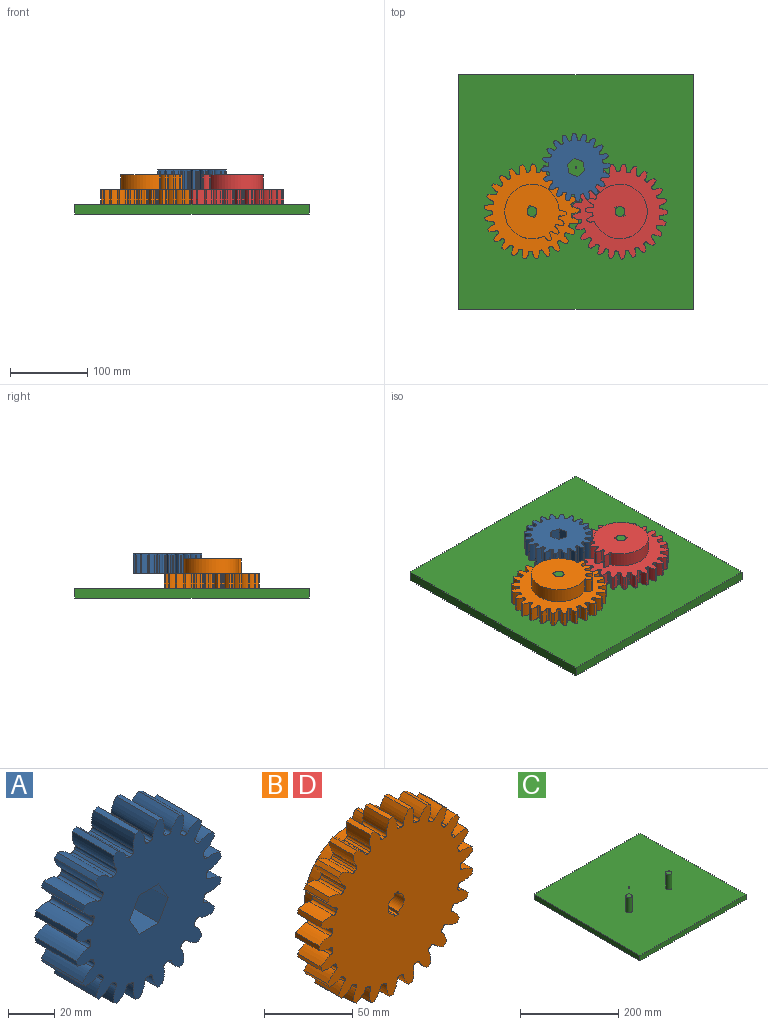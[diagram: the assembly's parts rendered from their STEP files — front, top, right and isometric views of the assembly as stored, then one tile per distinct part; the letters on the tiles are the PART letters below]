
ASSEMBLY  parts=4 mates=3
PART A: 128 faces, bbox 88.3x25.4x88.3 mm
  f0: plane 88.27x88.27mm, normal (0,-1,0), area 4657.8mm2, adj f2,f3,f4,f5,f6,f7,f8,f9
  f1: plane 88.27x88.27mm, normal (0,1,0), area 4657.8mm2, adj f2,f3,f4,f5,f6,f7,f8,f9
  f2: extruded ~25.4x7.35mm, area 207.9mm2, adj f0,f1,f81,f82
  f3: cylinder r=35.36mm len=25.4mm, axis (0,1,0), area 41mm2, adj f0,f1,f82,f83
  f4: extruded ~25.4x7.35mm, area 207.9mm2, adj f0,f1,f5,f83
  f5: cylinder r=44.45mm len=25.4mm, axis (0,1,0), area 71.3mm2, adj f0,f1,f4,f6
  f6: extruded ~25.4x7.98mm, area 207.9mm2, adj f0,f1,f5,f84
  f7: cylinder r=35.36mm len=25.4mm, axis (0,1,0), area 41mm2, adj f0,f1,f84,f85
  f8: extruded ~25.4x5.99mm, area 207.9mm2, adj f0,f1,f9,f85
  f9: cylinder r=44.45mm len=25.4mm, axis (0,1,0), area 71.3mm2, adj f0,f1,f8,f10
  f10: extruded ~25.4x7.84mm, area 207.9mm2, adj f0,f1,f9,f86
  f11: cylinder r=35.36mm len=25.4mm, axis (0,1,0), area 41mm2, adj f0,f1,f86,f87
  f12: extruded ~25.4x6.93mm, area 207.9mm2, adj f0,f1,f13,f87
  f13: cylinder r=44.45mm len=25.4mm, axis (0,1,0), area 71.3mm2, adj f0,f1,f12,f14
  f14: extruded ~25.4x6.93mm, area 207.9mm2, adj f0,f1,f13,f88
  f15: cylinder r=35.36mm len=25.4mm, axis (0,1,0), area 41mm2, adj f0,f1,f88,f89
  f16: extruded ~25.4x7.84mm, area 207.9mm2, adj f0,f1,f17,f89
  f17: cylinder r=44.45mm len=25.4mm, axis (0,1,0), area 71.3mm2, adj f0,f1,f16,f18
  f18: extruded ~25.4x5.99mm, area 207.9mm2, adj f0,f1,f17,f90
  f19: cylinder r=35.36mm len=25.4mm, axis (0,1,0), area 41mm2, adj f0,f1,f90,f91
  f20: extruded ~25.4x7.98mm, area 207.9mm2, adj f0,f1,f21,f91
  f21: cylinder r=44.45mm len=25.4mm, axis (0,1,0), area 71.3mm2, adj f0,f1,f20,f22
  f22: extruded ~25.4x7.35mm, area 207.9mm2, adj f0,f1,f21,f92
  f23: cylinder r=35.36mm len=25.4mm, axis (0,1,0), area 41mm2, adj f0,f1,f92,f93
  f24: extruded ~25.4x7.35mm, area 207.9mm2, adj f0,f1,f25,f93
  f25: cylinder r=44.45mm len=25.4mm, axis (0,1,0), area 71.3mm2, adj f0,f1,f24,f26
  f26: extruded ~25.4x7.98mm, area 207.9mm2, adj f0,f1,f25,f94
  f27: cylinder r=35.36mm len=25.4mm, axis (0,1,0), area 41mm2, adj f0,f1,f94,f95
  f28: extruded ~25.4x5.99mm, area 207.9mm2, adj f0,f1,f29,f95
  f29: cylinder r=44.45mm len=25.4mm, axis (0,1,0), area 71.3mm2, adj f0,f1,f28,f30
  f30: extruded ~25.4x7.84mm, area 207.9mm2, adj f0,f1,f29,f96
  f31: cylinder r=35.36mm len=25.4mm, axis (0,1,0), area 41mm2, adj f0,f1,f96,f97
  f32: extruded ~25.4x6.93mm, area 207.9mm2, adj f0,f1,f33,f97
  f33: cylinder r=44.45mm len=25.4mm, axis (0,1,0), area 71.3mm2, adj f0,f1,f32,f34
  f34: extruded ~25.4x6.93mm, area 207.9mm2, adj f0,f1,f33,f98
  f35: cylinder r=35.36mm len=25.4mm, axis (0,1,0), area 41mm2, adj f0,f1,f98,f99
  f36: extruded ~25.4x7.84mm, area 207.9mm2, adj f0,f1,f37,f99
  f37: cylinder r=44.45mm len=25.4mm, axis (0,1,0), area 71.3mm2, adj f0,f1,f36,f38
  f38: extruded ~25.4x5.99mm, area 207.9mm2, adj f0,f1,f37,f100
  f39: cylinder r=35.36mm len=25.4mm, axis (0,1,0), area 41mm2, adj f0,f1,f100,f101
  f40: extruded ~25.4x7.98mm, area 207.9mm2, adj f0,f1,f41,f101
  f41: cylinder r=44.45mm len=25.4mm, axis (0,1,0), area 71.3mm2, adj f0,f1,f40,f42
  f42: extruded ~25.4x7.35mm, area 207.9mm2, adj f0,f1,f41,f102
  f43: cylinder r=35.36mm len=25.4mm, axis (0,1,0), area 41mm2, adj f0,f1,f102,f103
  f44: extruded ~25.4x7.35mm, area 207.9mm2, adj f0,f1,f45,f103
  f45: cylinder r=44.45mm len=25.4mm, axis (0,1,0), area 71.3mm2, adj f0,f1,f44,f46
  f46: extruded ~25.4x7.98mm, area 207.9mm2, adj f0,f1,f45,f104
  f47: cylinder r=35.36mm len=25.4mm, axis (0,1,0), area 41mm2, adj f0,f1,f104,f105
  f48: extruded ~25.4x5.99mm, area 207.9mm2, adj f0,f1,f49,f105
  f49: cylinder r=44.45mm len=25.4mm, axis (0,1,0), area 71.3mm2, adj f0,f1,f48,f50
  f50: extruded ~25.4x7.84mm, area 207.9mm2, adj f0,f1,f49,f106
  f51: cylinder r=35.36mm len=25.4mm, axis (0,1,0), area 41mm2, adj f0,f1,f106,f107
  f52: extruded ~25.4x6.93mm, area 207.9mm2, adj f0,f1,f53,f107
  f53: cylinder r=44.45mm len=25.4mm, axis (0,1,0), area 71.3mm2, adj f0,f1,f52,f54
  f54: extruded ~25.4x6.93mm, area 207.9mm2, adj f0,f1,f53,f108
  f55: cylinder r=35.36mm len=25.4mm, axis (0,1,0), area 41mm2, adj f0,f1,f108,f109
  f56: extruded ~25.4x7.84mm, area 207.9mm2, adj f0,f1,f57,f109
  f57: cylinder r=44.45mm len=25.4mm, axis (0,1,0), area 71.3mm2, adj f0,f1,f56,f58
  f58: extruded ~25.4x5.99mm, area 207.9mm2, adj f0,f1,f57,f110
  f59: cylinder r=35.36mm len=25.4mm, axis (0,1,0), area 41mm2, adj f0,f1,f110,f111
  f60: extruded ~25.4x7.98mm, area 207.9mm2, adj f0,f1,f61,f111
  f61: cylinder r=44.45mm len=25.4mm, axis (0,1,0), area 71.3mm2, adj f0,f1,f60,f62
  f62: extruded ~25.4x7.35mm, area 207.9mm2, adj f0,f1,f61,f112
  f63: cylinder r=35.36mm len=25.4mm, axis (0,1,0), area 41mm2, adj f0,f1,f112,f113
  f64: extruded ~25.4x7.35mm, area 207.9mm2, adj f0,f1,f65,f113
  f65: cylinder r=44.45mm len=25.4mm, axis (0,1,0), area 71.3mm2, adj f0,f1,f64,f66
  f66: extruded ~25.4x7.98mm, area 207.9mm2, adj f0,f1,f65,f114
  f67: cylinder r=35.36mm len=25.4mm, axis (0,1,0), area 41mm2, adj f0,f1,f114,f115
  f68: extruded ~25.4x5.99mm, area 207.9mm2, adj f0,f1,f69,f115
  f69: cylinder r=44.45mm len=25.4mm, axis (0,1,0), area 71.3mm2, adj f0,f1,f68,f70
  f70: extruded ~25.4x7.84mm, area 207.9mm2, adj f0,f1,f69,f116
  f71: cylinder r=35.36mm len=25.4mm, axis (0,1,0), area 41mm2, adj f0,f1,f116,f117
  f72: extruded ~25.4x6.93mm, area 207.9mm2, adj f0,f1,f73,f117
  f73: cylinder r=44.45mm len=25.4mm, axis (0,1,0), area 71.3mm2, adj f0,f1,f72,f74
  f74: extruded ~25.4x6.93mm, area 207.9mm2, adj f0,f1,f73,f118
  f75: cylinder r=35.36mm len=25.4mm, axis (0,1,0), area 41mm2, adj f0,f1,f118,f119
  f76: extruded ~25.4x7.84mm, area 207.9mm2, adj f0,f1,f77,f119
  f77: cylinder r=44.45mm len=25.4mm, axis (0,1,0), area 71.3mm2, adj f0,f1,f76,f78
  f78: extruded ~25.4x5.99mm, area 207.9mm2, adj f0,f1,f77,f120
  f79: cylinder r=35.36mm len=25.4mm, axis (0,1,0), area 41mm2, adj f0,f1,f120,f121
  f80: extruded ~25.4x7.98mm, area 207.9mm2, adj f0,f1,f81,f121
  f81: cylinder r=44.45mm len=25.4mm, axis (0,1,0), area 71.3mm2, adj f0,f1,f2,f80
  f82: cylinder r=1.5mm len=25.4mm, axis (0,1,0), area 58.3mm2, adj f0,f1,f2,f3
  f83: cylinder r=1.5mm len=25.4mm, axis (0,1,0), area 58.3mm2, adj f0,f1,f3,f4
  f84: cylinder r=1.5mm len=25.4mm, axis (0,1,0), area 58.3mm2, adj f0,f1,f6,f7
  f85: cylinder r=1.5mm len=25.4mm, axis (0,1,0), area 58.3mm2, adj f0,f1,f7,f8
  f86: cylinder r=1.5mm len=25.4mm, axis (0,1,0), area 58.3mm2, adj f0,f1,f10,f11
  f87: cylinder r=1.5mm len=25.4mm, axis (0,1,0), area 58.3mm2, adj f0,f1,f11,f12
  f88: cylinder r=1.5mm len=25.4mm, axis (0,1,0), area 58.3mm2, adj f0,f1,f14,f15
  f89: cylinder r=1.5mm len=25.4mm, axis (0,1,0), area 58.3mm2, adj f0,f1,f15,f16
  f90: cylinder r=1.5mm len=25.4mm, axis (0,1,0), area 58.3mm2, adj f0,f1,f18,f19
  f91: cylinder r=1.5mm len=25.4mm, axis (0,1,0), area 58.3mm2, adj f0,f1,f19,f20
  f92: cylinder r=1.5mm len=25.4mm, axis (0,1,0), area 58.3mm2, adj f0,f1,f22,f23
  f93: cylinder r=1.5mm len=25.4mm, axis (0,1,0), area 58.3mm2, adj f0,f1,f23,f24
  f94: cylinder r=1.5mm len=25.4mm, axis (0,1,0), area 58.3mm2, adj f0,f1,f26,f27
  f95: cylinder r=1.5mm len=25.4mm, axis (0,1,0), area 58.3mm2, adj f0,f1,f27,f28
  f96: cylinder r=1.5mm len=25.4mm, axis (0,1,0), area 58.3mm2, adj f0,f1,f30,f31
  f97: cylinder r=1.5mm len=25.4mm, axis (0,1,0), area 58.3mm2, adj f0,f1,f31,f32
  f98: cylinder r=1.5mm len=25.4mm, axis (0,1,0), area 58.3mm2, adj f0,f1,f34,f35
  f99: cylinder r=1.5mm len=25.4mm, axis (0,1,0), area 58.3mm2, adj f0,f1,f35,f36
  f100: cylinder r=1.5mm len=25.4mm, axis (0,1,0), area 58.3mm2, adj f0,f1,f38,f39
  f101: cylinder r=1.5mm len=25.4mm, axis (0,1,0), area 58.3mm2, adj f0,f1,f39,f40
  f102: cylinder r=1.5mm len=25.4mm, axis (0,1,0), area 58.3mm2, adj f0,f1,f42,f43
  f103: cylinder r=1.5mm len=25.4mm, axis (0,1,0), area 58.3mm2, adj f0,f1,f43,f44
  f104: cylinder r=1.5mm len=25.4mm, axis (0,1,0), area 58.3mm2, adj f0,f1,f46,f47
  f105: cylinder r=1.5mm len=25.4mm, axis (0,1,0), area 58.3mm2, adj f0,f1,f47,f48
  f106: cylinder r=1.5mm len=25.4mm, axis (0,1,0), area 58.3mm2, adj f0,f1,f50,f51
  f107: cylinder r=1.5mm len=25.4mm, axis (0,1,0), area 58.3mm2, adj f0,f1,f51,f52
  f108: cylinder r=1.5mm len=25.4mm, axis (0,1,0), area 58.3mm2, adj f0,f1,f54,f55
  f109: cylinder r=1.5mm len=25.4mm, axis (0,1,0), area 58.3mm2, adj f0,f1,f55,f56
  f110: cylinder r=1.5mm len=25.4mm, axis (0,1,0), area 58.3mm2, adj f0,f1,f58,f59
  f111: cylinder r=1.5mm len=25.4mm, axis (0,1,0), area 58.3mm2, adj f0,f1,f59,f60
  f112: cylinder r=1.5mm len=25.4mm, axis (0,1,0), area 58.3mm2, adj f0,f1,f62,f63
  f113: cylinder r=1.5mm len=25.4mm, axis (0,1,0), area 58.3mm2, adj f0,f1,f63,f64
  f114: cylinder r=1.5mm len=25.4mm, axis (0,1,0), area 58.3mm2, adj f0,f1,f66,f67
  f115: cylinder r=1.5mm len=25.4mm, axis (0,1,0), area 58.3mm2, adj f0,f1,f67,f68
  f116: cylinder r=1.5mm len=25.4mm, axis (0,1,0), area 58.3mm2, adj f0,f1,f70,f71
  f117: cylinder r=1.5mm len=25.4mm, axis (0,1,0), area 58.3mm2, adj f0,f1,f71,f72
  f118: cylinder r=1.5mm len=25.4mm, axis (0,1,0), area 58.3mm2, adj f0,f1,f74,f75
  f119: cylinder r=1.5mm len=25.4mm, axis (0,1,0), area 58.3mm2, adj f0,f1,f75,f76
  f120: cylinder r=1.5mm len=25.4mm, axis (0,1,0), area 58.3mm2, adj f0,f1,f78,f79
  f121: cylinder r=1.5mm len=25.4mm, axis (0,1,0), area 58.3mm2, adj f0,f1,f79,f80
  f122: plane 25.4x11.88mm, normal (0,0,-1), area 301.7mm2, adj f0,f1,f123,f127
  f123: plane 25.4x10.29mm, normal (-0.87,0,-0.5), area 301.7mm2, adj f0,f1,f122,f124
  f124: plane 25.4x10.29mm, normal (-0.87,0,0.5), area 301.7mm2, adj f0,f1,f123,f125
  f125: plane 25.4x11.88mm, normal (0,0,1), area 301.7mm2, adj f0,f1,f124,f126
  f126: plane 25.4x10.29mm, normal (0.87,0,0.5), area 301.7mm2, adj f0,f1,f125,f127
  f127: plane 25.4x10.29mm, normal (0.87,0,-0.5), area 301.7mm2, adj f0,f1,f122,f126
PART B: 185 faces, bbox 123.2x38.1x123.4 mm
  f0: plane 79.49x75.61mm, normal (0,1,0), area 4006.1mm2, adj f1,f2,f3,f4,f5,f6,f7,f8
  f1: extruded ~19.05x5.99mm, area 155.9mm2, adj f0,f2,f17,f33
  f2: cylinder r=44.45mm len=19.05mm, axis (0,-1,0), area 53.5mm2, adj f0,f1,f3,f33
  f3: extruded ~19.05x7.84mm, area 155.9mm2, adj f0,f2,f18,f33
  f4: cylinder r=35.36mm len=19.05mm, axis (0,-1,0), area 30.7mm2, adj f0,f18,f19,f33
  f5: extruded ~19.05x6.93mm, area 155.9mm2, adj f0,f6,f19,f33
  f6: cylinder r=44.45mm len=19.05mm, axis (0,-1,0), area 53.5mm2, adj f0,f5,f7,f33
  f7: extruded ~19.05x6.93mm, area 155.9mm2, adj f0,f6,f20,f33
  f8: cylinder r=35.36mm len=19.05mm, axis (0,-1,0), area 30.7mm2, adj f0,f20,f21,f33
  f9: extruded ~19.05x7.84mm, area 155.9mm2, adj f0,f10,f21,f33
  f10: cylinder r=44.45mm len=19.05mm, axis (0,-1,0), area 53.5mm2, adj f0,f9,f11,f33
  f11: extruded ~19.05x5.99mm, area 155.9mm2, adj f0,f10,f22,f33
  f12: cylinder r=35.36mm len=19.05mm, axis (0,-1,0), area 30.7mm2, adj f0,f22,f23,f33
  f13: extruded ~19.05x7.98mm, area 155.9mm2, adj f0,f14,f23,f33
  f14: cylinder r=44.45mm len=19.05mm, axis (0,-1,0), area 53.5mm2, adj f0,f13,f15,f33
  f15: extruded ~19.05x7.35mm, area 155.9mm2, adj f0,f14,f24,f33
  f16: cylinder r=35.36mm len=70.72mm, axis (0,-1,0), area 3416.6mm2, adj f0,f17,f24,f33
  f17: cylinder r=1.5mm len=19.05mm, axis (0,-1,0), area 43.7mm2, adj f0,f1,f16,f33
  f18: cylinder r=1.5mm len=19.05mm, axis (0,-1,0), area 43.7mm2, adj f0,f3,f4,f33
  f19: cylinder r=1.5mm len=19.05mm, axis (0,-1,0), area 43.7mm2, adj f0,f4,f5,f33
  f20: cylinder r=1.5mm len=19.05mm, axis (0,-1,0), area 43.7mm2, adj f0,f7,f8,f33
  f21: cylinder r=1.5mm len=19.05mm, axis (0,-1,0), area 43.7mm2, adj f0,f8,f9,f33
  f22: cylinder r=1.5mm len=19.05mm, axis (0,-1,0), area 43.7mm2, adj f0,f11,f12,f33
  f23: cylinder r=1.5mm len=19.05mm, axis (0,-1,0), area 43.7mm2, adj f0,f12,f13,f33
  f24: cylinder r=1.5mm len=19.05mm, axis (0,-1,0), area 43.7mm2, adj f0,f15,f16,f33
  f25: plane 38.1x1.69mm, normal (-1,0,0), area 64.3mm2, adj f0,f26,f32,f34
  f26: cylinder r=6.45mm len=38.1mm, axis (0,1,0), area 646.1mm2, adj f0,f25,f27,f34
  f27: plane 38.1x1.69mm, normal (-1,0,0), area 64.3mm2, adj f0,f26,f28,f34
  f28: plane 38.1x3.28mm, normal (0,0,1), area 124.8mm2, adj f0,f27,f29,f34
  f29: plane 38.1x1.69mm, normal (1,0,0), area 64.3mm2, adj f0,f28,f30,f34
  f30: cylinder r=6.45mm len=38.1mm, axis (0,1,0), area 646.1mm2, adj f0,f29,f31,f34
  f31: plane 38.1x1.69mm, normal (1,0,0), area 64.3mm2, adj f0,f30,f32,f34
  f32: plane 38.1x3.28mm, normal (0,0,-1), area 124.8mm2, adj f0,f25,f31,f34
  f33: plane 123.39x123.16mm, normal (0,1,0), area 5959.4mm2, adj f1,f2,f3,f4,f5,f6,f7,f8
  f34: plane 123.39x123.16mm, normal (0,-1,0), area 9965.5mm2, adj f25,f26,f27,f28,f29,f30,f31,f32
  f35: extruded ~19.05x8.43mm, area 176.6mm2, adj f33,f34,f134,f135
  f36: cylinder r=51.44mm len=19.05mm, axis (0,1,0), area 33.1mm2, adj f33,f34,f135,f136
  f37: extruded ~19.05x8.43mm, area 176.6mm2, adj f33,f34,f38,f136
  f38: cylinder r=61.72mm len=19.05mm, axis (0,1,0), area 62.6mm2, adj f33,f34,f37,f39
  f39: extruded ~19.05x9.05mm, area 176.6mm2, adj f33,f34,f38,f137
  f40: cylinder r=51.44mm len=19.05mm, axis (0,1,0), area 33.1mm2, adj f33,f34,f137,f138
  f41: extruded ~19.05x7.28mm, area 176.6mm2, adj f33,f34,f42,f138
  f42: cylinder r=61.72mm len=19.05mm, axis (0,1,0), area 62.6mm2, adj f33,f34,f41,f43
  f43: extruded ~19.05x9.11mm, area 176.6mm2, adj f33,f34,f42,f139
  f44: cylinder r=51.44mm len=19.05mm, axis (0,1,0), area 33.1mm2, adj f33,f34,f139,f140
  f45: extruded ~19.05x7.19mm, area 176.6mm2, adj f33,f34,f46,f140
  f46: cylinder r=61.72mm len=19.05mm, axis (0,1,0), area 62.6mm2, adj f33,f34,f45,f47
  f47: extruded ~19.05x8.59mm, area 176.6mm2, adj f33,f34,f46,f141
  f48: cylinder r=51.44mm len=19.05mm, axis (0,1,0), area 33.1mm2, adj f33,f34,f141,f142
  f49: extruded ~19.05x8.37mm, area 176.6mm2, adj f33,f34,f50,f142
  f50: cylinder r=61.72mm len=19.05mm, axis (0,1,0), area 62.6mm2, adj f33,f34,f49,f51
  f51: extruded ~19.05x7.53mm, area 176.6mm2, adj f33,f34,f50,f143
  f52: cylinder r=51.44mm len=19.05mm, axis (0,1,0), area 33.1mm2, adj f33,f34,f143,f144
  f53: extruded ~19.05x9.03mm, area 176.6mm2, adj f33,f34,f54,f144
  f54: cylinder r=61.72mm len=19.05mm, axis (0,1,0), area 62.6mm2, adj f33,f34,f53,f55
  f55: extruded ~19.05x6.92mm, area 176.6mm2, adj f33,f34,f54,f145
  f56: cylinder r=51.44mm len=19.05mm, axis (0,1,0), area 33.1mm2, adj f33,f34,f145,f146
  f57: extruded ~19.05x9.12mm, area 176.6mm2, adj f33,f34,f58,f146
  f58: cylinder r=61.72mm len=19.05mm, axis (0,1,0), area 62.6mm2, adj f33,f34,f57,f59
  f59: extruded ~19.05x8.19mm, area 176.6mm2, adj f33,f34,f58,f147
  f60: cylinder r=51.44mm len=19.05mm, axis (0,1,0), area 33.1mm2, adj f33,f34,f147,f148
  f61: extruded ~19.05x8.64mm, area 176.6mm2, adj f33,f34,f62,f148
  f62: cylinder r=61.72mm len=19.05mm, axis (0,1,0), area 62.6mm2, adj f33,f34,f61,f63
  f63: extruded ~19.05x8.95mm, area 176.6mm2, adj f33,f34,f62,f149
  f64: cylinder r=51.44mm len=19.05mm, axis (0,1,0), area 33.1mm2, adj f33,f34,f149,f150
  f65: extruded ~19.05x7.61mm, area 176.6mm2, adj f33,f34,f66,f150
  f66: cylinder r=61.72mm len=19.05mm, axis (0,1,0), area 62.6mm2, adj f33,f34,f65,f67
  f67: extruded ~19.05x9.15mm, area 176.6mm2, adj f33,f34,f66,f151
  f68: cylinder r=51.44mm len=19.05mm, axis (0,1,0), area 33.1mm2, adj f33,f34,f151,f152
  f69: extruded ~19.05x6.82mm, area 176.6mm2, adj f33,f34,f70,f152
  f70: cylinder r=61.72mm len=19.05mm, axis (0,1,0), area 62.6mm2, adj f33,f34,f69,f71
  f71: extruded ~19.05x8.77mm, area 176.6mm2, adj f33,f34,f70,f153
  f72: cylinder r=51.44mm len=19.05mm, axis (0,1,0), area 33.1mm2, adj f33,f34,f153,f154
  f73: extruded ~19.05x8.12mm, area 176.6mm2, adj f33,f34,f74,f154
  f74: cylinder r=61.72mm len=19.05mm, axis (0,1,0), area 62.6mm2, adj f33,f34,f73,f75
  f75: extruded ~19.05x7.84mm, area 176.6mm2, adj f33,f34,f74,f155
  f76: cylinder r=51.44mm len=19.05mm, axis (0,1,0), area 33.1mm2, adj f33,f34,f155,f156
  f77: extruded ~19.05x8.92mm, area 176.6mm2, adj f33,f34,f78,f156
  f78: cylinder r=61.72mm len=19.05mm, axis (0,1,0), area 62.6mm2, adj f33,f34,f77,f79
  f79: extruded ~19.05x6.52mm, area 176.6mm2, adj f33,f34,f78,f157
  f80: cylinder r=51.44mm len=19.05mm, axis (0,1,0), area 33.1mm2, adj f33,f34,f157,f158
  f81: extruded ~19.05x9.15mm, area 176.6mm2, adj f33,f34,f82,f158
  f82: cylinder r=61.72mm len=19.05mm, axis (0,1,0), area 62.6mm2, adj f33,f34,f81,f83
  f83: extruded ~19.05x7.92mm, area 176.6mm2, adj f33,f34,f82,f159
  f84: cylinder r=51.44mm len=19.05mm, axis (0,1,0), area 33.1mm2, adj f33,f34,f159,f160
  f85: extruded ~19.05x8.81mm, area 176.6mm2, adj f33,f34,f86,f160
  f86: cylinder r=61.72mm len=19.05mm, axis (0,1,0), area 62.6mm2, adj f33,f34,f85,f87
  f87: extruded ~19.05x8.81mm, area 176.6mm2, adj f33,f34,f86,f161
  f88: cylinder r=51.44mm len=19.05mm, axis (0,1,0), area 33.1mm2, adj f33,f34,f161,f162
  f89: extruded ~19.05x7.92mm, area 176.6mm2, adj f33,f34,f90,f162
  f90: cylinder r=61.72mm len=19.05mm, axis (0,1,0), area 62.6mm2, adj f33,f34,f89,f91
  f91: extruded ~19.05x9.15mm, area 176.6mm2, adj f33,f34,f90,f163
  f92: cylinder r=51.44mm len=19.05mm, axis (0,1,0), area 33.1mm2, adj f33,f34,f163,f164
  f93: extruded ~19.05x6.52mm, area 176.6mm2, adj f33,f34,f94,f164
  f94: cylinder r=61.72mm len=19.05mm, axis (0,1,0), area 62.6mm2, adj f33,f34,f93,f95
  f95: extruded ~19.05x8.92mm, area 176.6mm2, adj f33,f34,f94,f165
  f96: cylinder r=51.44mm len=19.05mm, axis (0,1,0), area 33.1mm2, adj f33,f34,f165,f166
  f97: extruded ~19.05x7.84mm, area 176.6mm2, adj f33,f34,f98,f166
  f98: cylinder r=61.72mm len=19.05mm, axis (0,1,0), area 62.6mm2, adj f33,f34,f97,f99
  f99: extruded ~19.05x8.12mm, area 176.6mm2, adj f33,f34,f98,f167
  f100: cylinder r=51.44mm len=19.05mm, axis (0,1,0), area 33.1mm2, adj f33,f34,f167,f168
  f101: extruded ~19.05x8.77mm, area 176.6mm2, adj f33,f34,f102,f168
  f102: cylinder r=61.72mm len=19.05mm, axis (0,1,0), area 62.6mm2, adj f33,f34,f101,f103
  f103: extruded ~19.05x6.82mm, area 176.6mm2, adj f33,f34,f102,f169
  f104: cylinder r=51.44mm len=19.05mm, axis (0,1,0), area 33.1mm2, adj f33,f34,f169,f170
  f105: extruded ~19.05x9.15mm, area 176.6mm2, adj f33,f34,f106,f170
  f106: cylinder r=61.72mm len=19.05mm, axis (0,1,0), area 62.6mm2, adj f33,f34,f105,f107
  f107: extruded ~19.05x7.61mm, area 176.6mm2, adj f33,f34,f106,f171
  f108: cylinder r=51.44mm len=19.05mm, axis (0,1,0), area 33.1mm2, adj f33,f34,f171,f172
  f109: extruded ~19.05x8.95mm, area 176.6mm2, adj f33,f34,f110,f172
  f110: cylinder r=61.72mm len=19.05mm, axis (0,1,0), area 62.6mm2, adj f33,f34,f109,f111
  f111: extruded ~19.05x8.64mm, area 176.6mm2, adj f33,f34,f110,f173
  f112: cylinder r=51.44mm len=19.05mm, axis (0,1,0), area 33.1mm2, adj f33,f34,f173,f174
  f113: extruded ~19.05x8.19mm, area 176.6mm2, adj f33,f34,f114,f174
  f114: cylinder r=61.72mm len=19.05mm, axis (0,1,0), area 62.6mm2, adj f33,f34,f113,f115
  f115: extruded ~19.05x9.12mm, area 176.6mm2, adj f33,f34,f114,f175
  f116: cylinder r=51.44mm len=19.05mm, axis (0,1,0), area 33.1mm2, adj f33,f34,f175,f176
  f117: extruded ~19.05x6.92mm, area 176.6mm2, adj f33,f34,f118,f176
  f118: cylinder r=61.72mm len=19.05mm, axis (0,1,0), area 62.6mm2, adj f33,f34,f117,f119
  f119: extruded ~19.05x9.03mm, area 176.6mm2, adj f33,f34,f118,f177
  f120: cylinder r=51.44mm len=19.05mm, axis (0,1,0), area 33.1mm2, adj f33,f34,f177,f178
  f121: extruded ~19.05x7.53mm, area 176.6mm2, adj f33,f34,f122,f178
  f122: cylinder r=61.72mm len=19.05mm, axis (0,1,0), area 62.6mm2, adj f33,f34,f121,f123
  f123: extruded ~19.05x8.37mm, area 176.6mm2, adj f33,f34,f122,f179
  f124: cylinder r=51.44mm len=19.05mm, axis (0,1,0), area 33.1mm2, adj f33,f34,f179,f180
  f125: extruded ~19.05x8.59mm, area 176.6mm2, adj f33,f34,f126,f180
  f126: cylinder r=61.72mm len=19.05mm, axis (0,1,0), area 62.6mm2, adj f33,f34,f125,f127
  f127: extruded ~19.05x7.19mm, area 176.6mm2, adj f33,f34,f126,f181
  f128: cylinder r=51.44mm len=19.05mm, axis (0,1,0), area 33.1mm2, adj f33,f34,f181,f182
  f129: extruded ~19.05x9.11mm, area 176.6mm2, adj f33,f34,f130,f182
  f130: cylinder r=61.72mm len=19.05mm, axis (0,1,0), area 62.6mm2, adj f33,f34,f129,f131
  f131: extruded ~19.05x7.28mm, area 176.6mm2, adj f33,f34,f130,f183
  f132: cylinder r=51.44mm len=19.05mm, axis (0,1,0), area 33.1mm2, adj f33,f34,f183,f184
  f133: extruded ~19.05x9.05mm, area 176.6mm2, adj f33,f34,f134,f184
  f134: cylinder r=61.72mm len=19.05mm, axis (0,1,0), area 62.6mm2, adj f33,f34,f35,f133
  f135: cylinder r=1.64mm len=19.05mm, axis (0,1,0), area 48.2mm2, adj f33,f34,f35,f36
  f136: cylinder r=1.64mm len=19.05mm, axis (0,1,0), area 48.2mm2, adj f33,f34,f36,f37
  f137: cylinder r=1.64mm len=19.05mm, axis (0,1,0), area 48.2mm2, adj f33,f34,f39,f40
  f138: cylinder r=1.64mm len=19.05mm, axis (0,1,0), area 48.2mm2, adj f33,f34,f40,f41
  f139: cylinder r=1.64mm len=19.05mm, axis (0,1,0), area 48.2mm2, adj f33,f34,f43,f44
  f140: cylinder r=1.64mm len=19.05mm, axis (0,1,0), area 48.2mm2, adj f33,f34,f44,f45
  f141: cylinder r=1.64mm len=19.05mm, axis (0,1,0), area 48.2mm2, adj f33,f34,f47,f48
  f142: cylinder r=1.64mm len=19.05mm, axis (0,1,0), area 48.2mm2, adj f33,f34,f48,f49
  f143: cylinder r=1.64mm len=19.05mm, axis (0,1,0), area 48.2mm2, adj f33,f34,f51,f52
  f144: cylinder r=1.64mm len=19.05mm, axis (0,1,0), area 48.2mm2, adj f33,f34,f52,f53
  f145: cylinder r=1.64mm len=19.05mm, axis (0,1,0), area 48.2mm2, adj f33,f34,f55,f56
  f146: cylinder r=1.64mm len=19.05mm, axis (0,1,0), area 48.2mm2, adj f33,f34,f56,f57
  f147: cylinder r=1.64mm len=19.05mm, axis (0,1,0), area 48.2mm2, adj f33,f34,f59,f60
  f148: cylinder r=1.64mm len=19.05mm, axis (0,1,0), area 48.2mm2, adj f33,f34,f60,f61
  f149: cylinder r=1.64mm len=19.05mm, axis (0,1,0), area 48.2mm2, adj f33,f34,f63,f64
  f150: cylinder r=1.64mm len=19.05mm, axis (0,1,0), area 48.2mm2, adj f33,f34,f64,f65
  f151: cylinder r=1.64mm len=19.05mm, axis (0,1,0), area 48.2mm2, adj f33,f34,f67,f68
  f152: cylinder r=1.64mm len=19.05mm, axis (0,1,0), area 48.2mm2, adj f33,f34,f68,f69
  f153: cylinder r=1.64mm len=19.05mm, axis (0,1,0), area 48.2mm2, adj f33,f34,f71,f72
  f154: cylinder r=1.64mm len=19.05mm, axis (0,1,0), area 48.2mm2, adj f33,f34,f72,f73
  f155: cylinder r=1.64mm len=19.05mm, axis (0,1,0), area 48.2mm2, adj f33,f34,f75,f76
  f156: cylinder r=1.64mm len=19.05mm, axis (0,1,0), area 48.2mm2, adj f33,f34,f76,f77
  f157: cylinder r=1.64mm len=19.05mm, axis (0,1,0), area 48.2mm2, adj f33,f34,f79,f80
  f158: cylinder r=1.64mm len=19.05mm, axis (0,1,0), area 48.2mm2, adj f33,f34,f80,f81
  f159: cylinder r=1.64mm len=19.05mm, axis (0,1,0), area 48.2mm2, adj f33,f34,f83,f84
  f160: cylinder r=1.64mm len=19.05mm, axis (0,1,0), area 48.2mm2, adj f33,f34,f84,f85
  f161: cylinder r=1.64mm len=19.05mm, axis (0,1,0), area 48.2mm2, adj f33,f34,f87,f88
  f162: cylinder r=1.64mm len=19.05mm, axis (0,1,0), area 48.2mm2, adj f33,f34,f88,f89
  f163: cylinder r=1.64mm len=19.05mm, axis (0,1,0), area 48.2mm2, adj f33,f34,f91,f92
  f164: cylinder r=1.64mm len=19.05mm, axis (0,1,0), area 48.2mm2, adj f33,f34,f92,f93
  f165: cylinder r=1.64mm len=19.05mm, axis (0,1,0), area 48.2mm2, adj f33,f34,f95,f96
  f166: cylinder r=1.64mm len=19.05mm, axis (0,1,0), area 48.2mm2, adj f33,f34,f96,f97
  f167: cylinder r=1.64mm len=19.05mm, axis (0,1,0), area 48.2mm2, adj f33,f34,f99,f100
  f168: cylinder r=1.64mm len=19.05mm, axis (0,1,0), area 48.2mm2, adj f33,f34,f100,f101
  f169: cylinder r=1.64mm len=19.05mm, axis (0,1,0), area 48.2mm2, adj f33,f34,f103,f104
  f170: cylinder r=1.64mm len=19.05mm, axis (0,1,0), area 48.2mm2, adj f33,f34,f104,f105
  f171: cylinder r=1.64mm len=19.05mm, axis (0,1,0), area 48.2mm2, adj f33,f34,f107,f108
  f172: cylinder r=1.64mm len=19.05mm, axis (0,1,0), area 48.2mm2, adj f33,f34,f108,f109
  f173: cylinder r=1.64mm len=19.05mm, axis (0,1,0), area 48.2mm2, adj f33,f34,f111,f112
  f174: cylinder r=1.64mm len=19.05mm, axis (0,1,0), area 48.2mm2, adj f33,f34,f112,f113
  f175: cylinder r=1.64mm len=19.05mm, axis (0,1,0), area 48.2mm2, adj f33,f34,f115,f116
  f176: cylinder r=1.64mm len=19.05mm, axis (0,1,0), area 48.2mm2, adj f33,f34,f116,f117
  f177: cylinder r=1.64mm len=19.05mm, axis (0,1,0), area 48.2mm2, adj f33,f34,f119,f120
  f178: cylinder r=1.64mm len=19.05mm, axis (0,1,0), area 48.2mm2, adj f33,f34,f120,f121
  f179: cylinder r=1.64mm len=19.05mm, axis (0,1,0), area 48.2mm2, adj f33,f34,f123,f124
  f180: cylinder r=1.64mm len=19.05mm, axis (0,1,0), area 48.2mm2, adj f33,f34,f124,f125
  f181: cylinder r=1.64mm len=19.05mm, axis (0,1,0), area 48.2mm2, adj f33,f34,f127,f128
  f182: cylinder r=1.64mm len=19.05mm, axis (0,1,0), area 48.2mm2, adj f33,f34,f128,f129
  f183: cylinder r=1.64mm len=19.05mm, axis (0,1,0), area 48.2mm2, adj f33,f34,f131,f132
  f184: cylinder r=1.64mm len=19.05mm, axis (0,1,0), area 48.2mm2, adj f33,f34,f132,f133
PART C: 12 faces, bbox 304.8x304.8x50.8 mm
  f0: plane 304.8x12.7mm, normal (0,-1,0), area 3871mm2, adj f1,f3,f4,f5
  f1: plane 304.8x12.7mm, normal (1,0,0), area 3871mm2, adj f0,f2,f4,f5
  f2: plane 304.8x12.7mm, normal (0,1,0), area 3871mm2, adj f1,f3,f4,f5
  f3: plane 304.8x12.7mm, normal (-1,0,0), area 3871mm2, adj f0,f2,f4,f5
  f4: plane 304.8x304.8mm, normal (0,0,1), area 92644.6mm2, adj f0,f1,f2,f3,f6,f8,f10
  f5: plane 304.8x304.8mm, normal (0,0,-1), area 92903mm2, adj f0,f1,f2,f3
  f6: cylinder r=6.35mm len=38.1mm, axis (0,0,-1), area 1520.1mm2, adj f4,f7
  f7: plane 12.7x12.7mm, normal (0,0,1), area 126.7mm2, adj f6
  f8: cylinder r=6.35mm len=38.1mm, axis (0,0,-1), area 1520.1mm2, adj f4,f9
  f9: plane 12.7x12.7mm, normal (0,0,1), area 126.7mm2, adj f8
  f10: cylinder r=1.27mm len=2.54mm, axis (0,0,-1), area 20.3mm2, adj f4,f11
  f11: plane 2.54x2.54mm, normal (0,0,1), area 5.1mm2, adj f10
PART D: same geometry as B
PLACE A rot(axis=(-0.66,0.53,-0.53),113.2deg) t=(-378.53,-4.69,279.02)mm
PLACE B rot(axis=(0.96,0.2,0.2),92.4deg) t=(-435.68,-61.85,279.02)mm
PLACE C t=(-226.13,-188.85,247.27)mm fixed
PLACE D rot(axis=(0.26,-0.68,-0.68),150.4deg) t=(-321.38,-61.85,279.02)mm
MATE revolute D.f30 <-> C.f8  axis (0,0,-1) through (-321.38,-61.85,259.97)mm
MATE revolute B.f26 <-> C.f6  axis (0,0,1) through (-435.68,-61.85,259.97)mm
MATE revolute A.f5 <-> C.f10  axis (0,0,-1) through (-378.53,-4.69,279.02)mm
